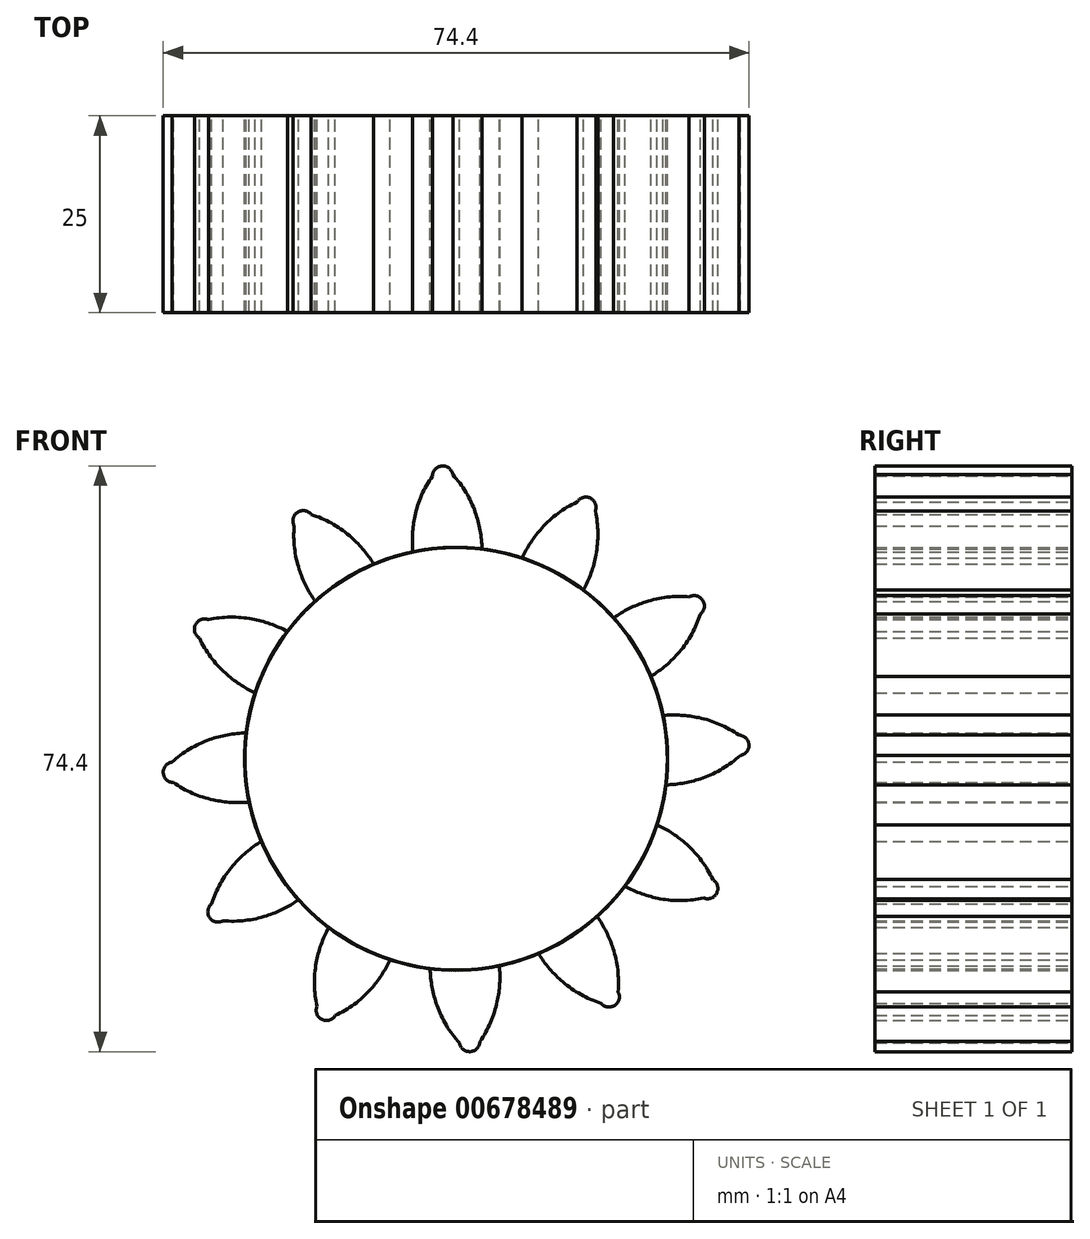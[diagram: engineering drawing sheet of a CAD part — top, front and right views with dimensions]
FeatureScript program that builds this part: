
annotation { "Feature Type Name" : "Feature", "Feature Type Description" : "" }
export const myFeature = defineFeature(function(context is Context, id is Id, definition is map)
    precondition{}
    {
        {
            var Q0;
            Q0=qCreatedBy(makeId("Front.planeOp"),FACE);
            var sketch = newSketch(context, id + "F0", { "sketchPlane" : qUnion([Q0])});
            skCircle(sketch, "E0", {"center": v(0, 0) * mm, "radius": 26.86 * mm});
            skCircle(sketch, "E1", {"center": v(0, 0) * mm, "radius": 29.34 * mm, "construction": true});
            skCircle(sketch, "E2", {"center": v(0, 0) * mm, "radius": 31.75 * mm, "construction": true});
            skCircle(sketch, "E3", {"center": v(-11.3, 26.33) * mm, "radius": 14.6 * mm, "construction": true});
            skArc(sketch, "E4", {"start": v(2.43, 31.33) * mm, "mid": v(1.24, 33.85) * mm, "end": v(-0.42, 36.09) * mm});
            skArc(sketch, "E5", {"start": v(3.31, 26.37) * mm, "mid": v(3.08, 28.88) * mm, "end": v(2.43, 31.33) * mm});
            skArc(sketch, "E6.MirrorCS", {"start": v(-5.23, 30.82) * mm, "mid": v(-4.38, 33.48) * mm, "end": v(-3.02, 35.92) * mm});
            skArc(sketch, "E7.MirrorCS", {"start": v(-5.45, 25.8) * mm, "mid": v(-5.55, 28.32) * mm, "end": v(-5.23, 30.82) * mm});
            skArc(sketch, "E8", {"start": v(-0.42, 36.09) * mm, "mid": v(-1.8, 37.2) * mm, "end": v(-3.02, 35.92) * mm});
            skSolve(sketch);
        }
        {
            var Q0;
            Q0=makeQuery(id+"F0.imprint","IMPRINT",FACE,{"disambiguationData":[TD([[makeQuery(id+"F0.imprint","IMPRINT",EDGE,{"derivedFrom":sQuery(id+"F0.wireOp",EDGE,"E0")}),1.0]])]});
            var Q1;
            {var subQ2=sQuery(id+"F0.wireOp",EDGE,"E4");Q1=makeQuery(id+"F0.imprint","IMPRINT",FACE,{"disambiguationData":[TD([[makeQuery(id+"F0.imprint","IMPRINT",EDGE,{"derivedFrom":subQ2}),1.0]])]});}
            extrude(context, id + "F1", {"entities" : qUnion([Q0, Q1]), "depth" : 25 * mm, "offsetDistance" : 25 * mm});
        }
        {
            var Q0;
            Q0=makeQuery(id+"F1.opExtrude","SWEPT_BODY",BODY,{"disambiguationData":[OSD([sQuery(id+"F0.wireOp",EDGE,"E0"),sQuery(id+"F0.wireOp",EDGE,"E4"),sQuery(id+"F0.wireOp",EDGE,"E5"),sQuery(id+"F0.wireOp",EDGE,"E6.MirrorCS"),sQuery(id+"F0.wireOp",EDGE,"E7.MirrorCS"),sQuery(id+"F0.wireOp",EDGE,"E8")])]});
            var Q1;
            Q1=makeQuery(id+"F1.opExtrude","SWEPT_FACE",FACE,{"disambiguationData":[OSD([sQuery(id+"F0.wireOp",EDGE,"E0")])]});
            circularPattern(context, id + "F2", {"entities" : qUnion([Q0]), "axis" : qUnion([Q1]), "angle" : 360 * degree, "instanceCount" : 12, "equalSpace" : true});
        }
    });
